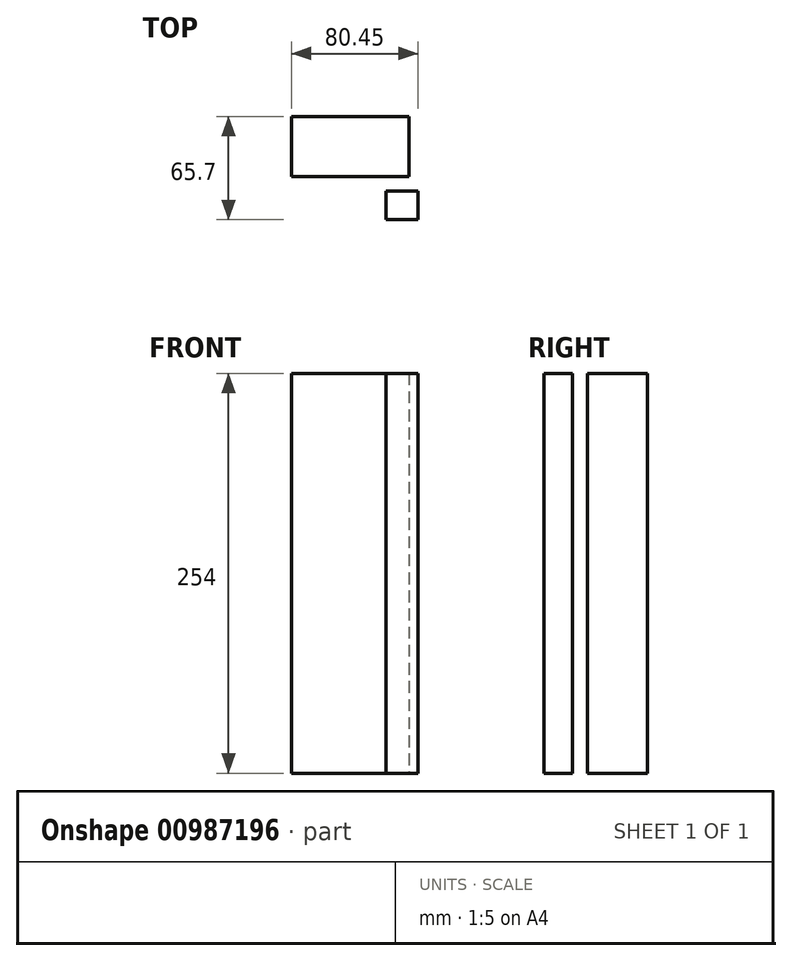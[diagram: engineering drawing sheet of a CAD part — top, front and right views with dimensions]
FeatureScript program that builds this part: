
annotation { "Feature Type Name" : "Feature", "Feature Type Description" : "" }
export const myFeature = defineFeature(function(context is Context, id is Id, definition is map)
    precondition{}
    {
        {
            var Q0;
            Q0=qCreatedBy(makeId("Top.planeOp"),FACE);
            var sketch = newSketch(context, id + "F0", { "sketchPlane" : qUnion([Q0])});
            skLineSegment(sketch, "E0.bottom", {"start": v(-37.38, 0) * mm, "end": v(37.38, 0) * mm});
            skLineSegment(sketch, "E0.top", {"start": v(-37.38, 38.26) * mm, "end": v(37.38, 38.26) * mm});
            skLineSegment(sketch, "E0.left", {"start": v(-37.38, 0) * mm, "end": v(-37.38, 38.26) * mm});
            skLineSegment(sketch, "E0.right", {"start": v(37.38, 0) * mm, "end": v(37.38, 38.26) * mm});
            skPoint(sketch, "E0.middle", {"position": v(0, 19.13) * mm});
            skLineSegment(sketch, "E1.bottom", {"start": v(22.52, -9.3) * mm, "end": v(43.07, -9.3) * mm});
            skLineSegment(sketch, "E1.top", {"start": v(22.52, -27.44) * mm, "end": v(43.07, -27.44) * mm});
            skLineSegment(sketch, "E1.left", {"start": v(22.52, -9.3) * mm, "end": v(22.52, -27.44) * mm});
            skLineSegment(sketch, "E1.right", {"start": v(43.07, -9.3) * mm, "end": v(43.07, -27.44) * mm});
            skSolve(sketch);
        }
        {
            var Q0;
            Q0=qSketchRegion(id+"F0",true);
            extrude(context, id + "F1", {"entities" : qUnion([Q0]), "depth" : 254 * mm, "offsetDistance" : 25.4 * mm});
        }
        {
            var Q0;
            Q0=qCreatedBy(makeId("Top.planeOp"),FACE);
            cPlane(context, id + "F2", {"entities" : qUnion([Q0]), "cplaneType" : CPlaneType.OFFSET, "offset" : 101.6 * mm, "width" : 152.4 * mm, "height" : 152.4 * mm});
        }
    });
